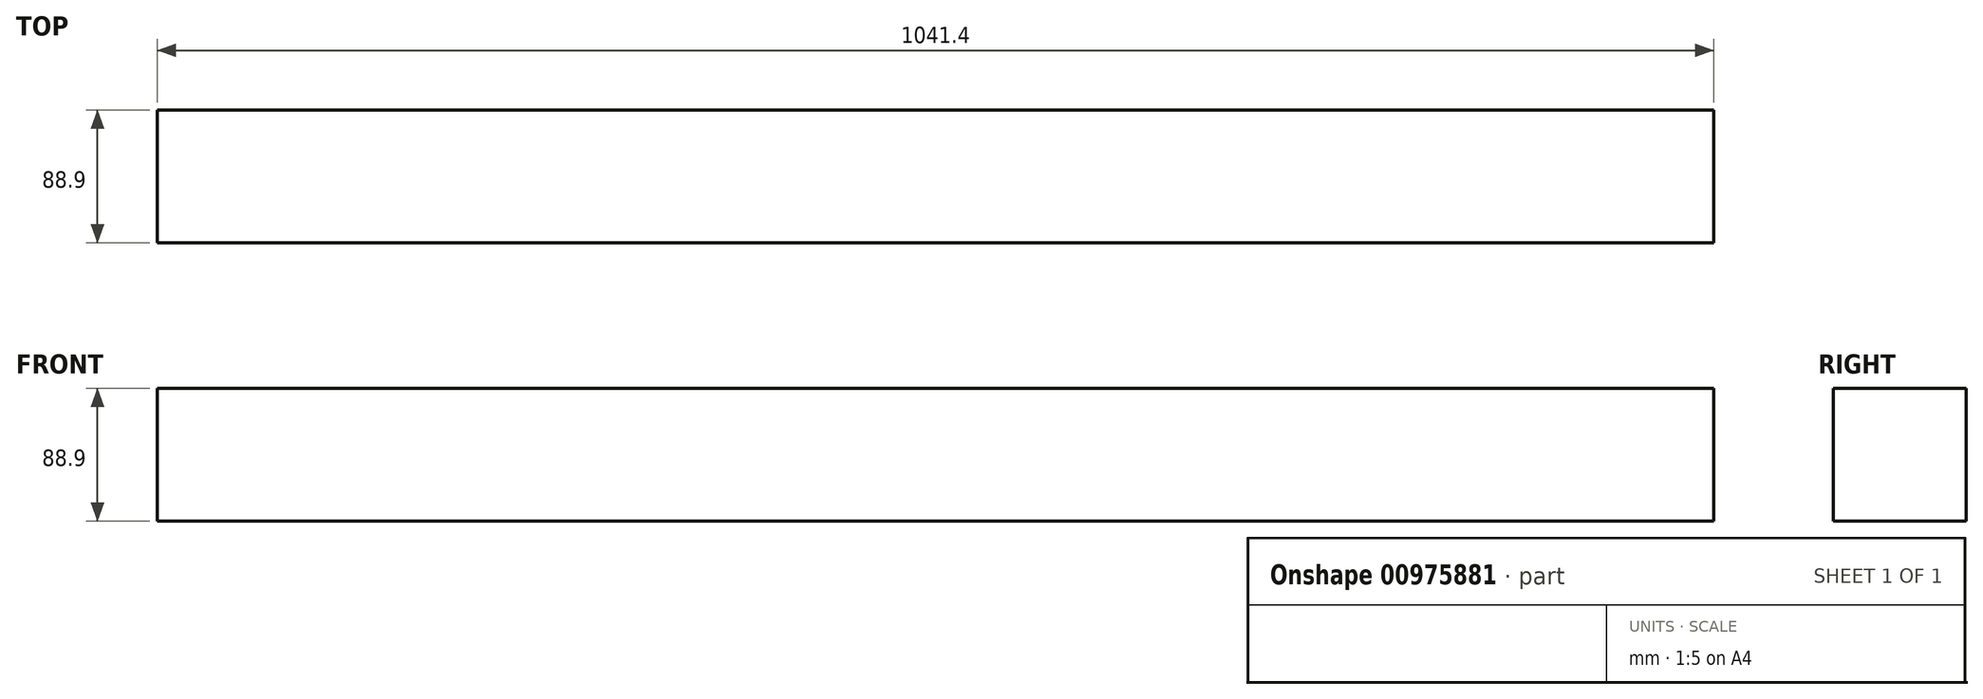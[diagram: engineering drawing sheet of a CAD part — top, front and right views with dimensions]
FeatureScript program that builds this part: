
annotation { "Feature Type Name" : "Feature", "Feature Type Description" : "" }
export const myFeature = defineFeature(function(context is Context, id is Id, definition is map)
    precondition{}
    {
        {
            var Q0;
            Q0=qCreatedBy(makeId("Right.planeOp"),FACE);
            var sketch = newSketch(context, id + "F0", { "sketchPlane" : qUnion([Q0])});
            skLineSegment(sketch, "E0.bottom", {"start": v(0, 0) * mm, "end": v(0, 0) * mm});
            skLineSegment(sketch, "E0.top", {"start": v(0, 0) * mm, "end": v(0, 0) * mm});
            skLineSegment(sketch, "E0.left", {"start": v(0, 0) * mm, "end": v(0, 0) * mm});
            skLineSegment(sketch, "E0.right", {"start": v(0, 0) * mm, "end": v(0, 0) * mm});
            skPoint(sketch, "E0.middle", {"position": v(0, 0) * mm});
            skLineSegment(sketch, "E1.bottom", {"start": v(44.45, 44.45) * mm, "end": v(-44.45, 44.45) * mm});
            skLineSegment(sketch, "E1.top", {"start": v(44.45, -44.45) * mm, "end": v(-44.45, -44.45) * mm});
            skLineSegment(sketch, "E1.left", {"start": v(44.45, 44.45) * mm, "end": v(44.45, -44.45) * mm});
            skLineSegment(sketch, "E1.right", {"start": v(-44.45, 44.45) * mm, "end": v(-44.45, -44.45) * mm});
            skSolve(sketch);
        }
        {
            var Q0;
            Q0 = qSketchRegion(id + "F0", true);
            extrude(context, id + "F1", {"entities" : qUnion([Q0]), "depth" : 1041.4 * mm, "offsetDistance" : 25.4 * mm});
        }
    });
